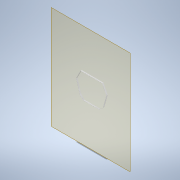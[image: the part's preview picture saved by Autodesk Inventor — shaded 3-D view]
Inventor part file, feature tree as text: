
AUTODESK INVENTOR PART (.ipt)
format: ipt  version: 2021 (Build 250183000, 183)  size: 483,840 bytes
history: native  units: in
note: dims shown in document units (in); Inventor stores cm internally (conversion verified against a paired STEP export)
features: other x5, plane x2, sketch x2, extrude x1, loft x1, reference x1
ambient origin geometry x8: Origin, YZ Plane, XZ Plane, XY Plane, X Axis, Y Axis, Z Axis, Center Point
bodies: Body1 (feature_tree), Body2 (feature_tree)
feature tree (12):
  plane  "Work Plane1"
  sketch  "Sketch1"  dims[d0=1.0in d1=0.0625in]
  extrude  "Extrusion2"  Depth=0.0625in
  plane  "Work Plane2"
  loft  "Loft1"
  reference  "Reference1"
  sketch  "Sketch2"  dims[d4=0.25in d5=0.25in d6=1.0in d7=0.0in d8=0.0in d9=90.0deg d10=0.0in d11=90.0deg]
  other  "<userpath>\Documents\FSAE\Lafayette-Motorsports\FullCarV2.0.iam"
  other  "FullCarV2.0.iam"
  other  "FullFrame.004:1"
  other  "Frame 1606066014995:1"
  other  "end body:1"
